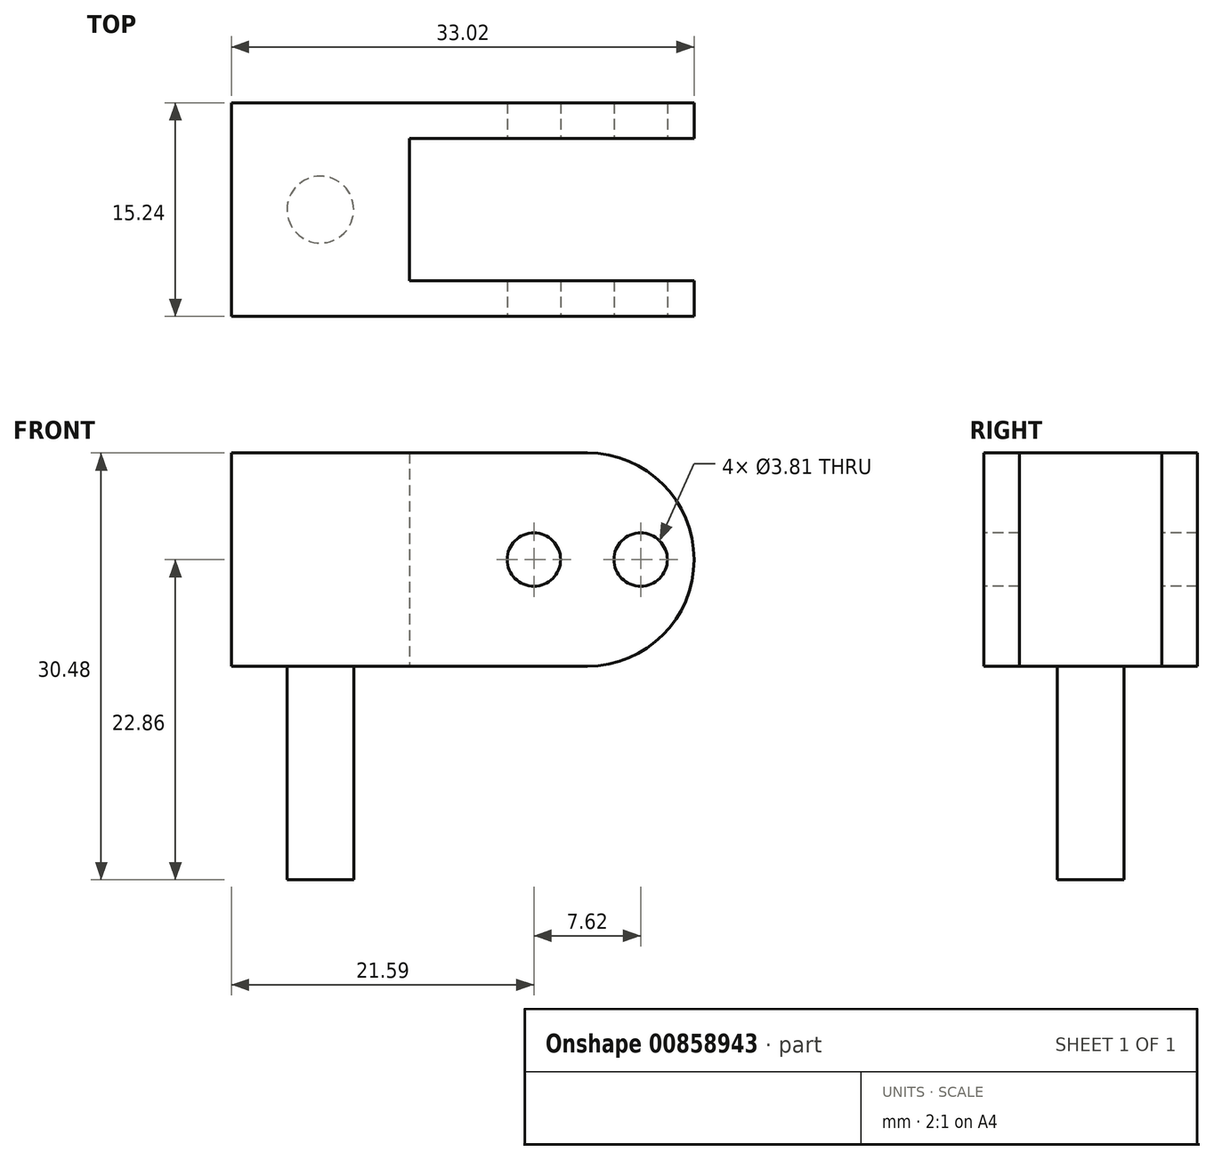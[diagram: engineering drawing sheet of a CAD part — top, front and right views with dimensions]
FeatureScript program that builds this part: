
annotation { "Feature Type Name" : "Feature", "Feature Type Description" : "" }
export const myFeature = defineFeature(function(context is Context, id is Id, definition is map)
    precondition{}
    {
        {
            var Q0;
            Q0=qCreatedBy(makeId("Top.planeOp"),FACE);
            var sketch = newSketch(context, id + "F0", { "sketchPlane" : qUnion([Q0])});
            skLineSegment(sketch, "E0.bottom", {"start": v(6.35, 7.62) * mm, "end": v(-6.35, 7.62) * mm});
            skLineSegment(sketch, "E0.top", {"start": v(6.35, -7.62) * mm, "end": v(-6.35, -7.62) * mm});
            skLineSegment(sketch, "E0.left", {"start": v(6.35, 7.62) * mm, "end": v(6.35, -7.62) * mm});
            skLineSegment(sketch, "E0.right", {"start": v(-6.35, 7.62) * mm, "end": v(-6.35, -7.62) * mm});
            skPoint(sketch, "E0.middle", {"position": v(0, 0) * mm});
            skSolve(sketch);
        }
        {
            var Q0;
            Q0=qSketchRegion(id+"F0",true);
            extrude(context, id + "F1", {"entities" : qUnion([Q0]), "depth" : 15.24 * mm, "offsetDistance" : 25.4 * mm});
        }
        {
            var Q0;
            Q0=makeQuery(id+"F1.opExtrude","CAP_FACE",FACE,{"disambiguationData":[OSD([sQuery(id+"F0.wireOp",EDGE,"E0.bottom"),sQuery(id+"F0.wireOp",EDGE,"E0.top"),sQuery(id+"F0.wireOp",EDGE,"E0.left"),sQuery(id+"F0.wireOp",EDGE,"E0.right")])],"isStart":true});
            var sketch = newSketch(context, id + "F2", { "sketchPlane" : qUnion([Q0])});
            skCircle(sketch, "E1", {"center": v(0, 0) * mm, "radius": 2.38 * mm});
            skSolve(sketch);
        }
        {
            var Q0;
            Q0=qSketchRegion(id+"F2",true);
            extrude(context, id + "F3", {"entities" : qUnion([Q0]), "operationType" : NewBodyOperationType.ADD, "depth" : 15.24 * mm, "offsetDistance" : 25.4 * mm});
        }
        {
            var Q0;
            Q0=makeQuery(id+"F1.opExtrude","SWEPT_FACE",FACE,{"disambiguationData":[OSD([sQuery(id+"F0.wireOp",EDGE,"E0.top")])]});
            var sketch = newSketch(context, id + "F4", { "sketchPlane" : qUnion([Q0])});
            skLineSegment(sketch, "E2.bottom", {"start": v(6.35, 15.24) * mm, "end": v(19.05, 15.24) * mm});
            skLineSegment(sketch, "E2.top", {"start": v(6.35, 0) * mm, "end": v(19.05, 0) * mm});
            skLineSegment(sketch, "E2.left", {"start": v(6.35, 15.24) * mm, "end": v(6.35, 0) * mm});
            skLineSegment(sketch, "E2.right", {"start": v(19.05, 15.24) * mm, "end": v(19.05, 0) * mm});
            skArc(sketch, "E3", {"start": v(19.05, 0) * mm, "mid": v(26.67, 7.62) * mm, "end": v(19.05, 15.24) * mm});
            skSolve(sketch);
        }
        {
            var Q0;
            Q0=makeQuery(id+"F4.imprint","IMPRINT",FACE,{"disambiguationData":[TD([[makeQuery(id+"F4.imprint","IMPRINT",EDGE,{"derivedFrom":sQuery(id+"F4.wireOp",EDGE,"E2.bottom")}),-1.0]])]});
            var Q1;
            Q1=makeQuery(id+"F4.imprint","IMPRINT",FACE,{"disambiguationData":[TD([[makeQuery(id+"F4.imprint","IMPRINT",EDGE,{"derivedFrom":sQuery(id+"F4.wireOp",EDGE,"E2.right")}),1.0]])]});
            extrude(context, id + "F5", {"entities" : qUnion([Q0, Q1]), "operationType" : NewBodyOperationType.ADD, "oppositeDirection" : true, "depth" : 2.54 * mm, "offsetDistance" : 25.4 * mm});
        }
        {
            var Q0;
            Q0=makeQuery(id+"F1.opExtrude","SWEPT_BODY",BODY,{"disambiguationData":[OSD([sQuery(id+"F0.wireOp",EDGE,"E0.bottom"),sQuery(id+"F0.wireOp",EDGE,"E0.top"),sQuery(id+"F0.wireOp",EDGE,"E0.left"),sQuery(id+"F0.wireOp",EDGE,"E0.right")])]});
            var Q1;
            Q1=qCreatedBy(makeId("Front.planeOp"),FACE);
            mirror(context, id + "F6", {"operationType" : NewBodyOperationType.ADD, "entities" : qUnion([Q0]), "mirrorPlane" : qUnion([Q1])});
        }
        {
            var Q0;
            Q0=makeQuery(id+"F5.boolean.opBoolean","MERGE",FACE,{"derivedFrom":[makeQuery(id+"F1.opExtrude","SWEPT_FACE",FACE,{"disambiguationData":[OSD([sQuery(id+"F0.wireOp",EDGE,"E0.top")])]}),makeQuery(id+"F5.opExtrude","CAP_FACE",FACE,{"disambiguationData":[OSD([sQuery(id+"F4.wireOp",EDGE,"E2.bottom"),sQuery(id+"F4.wireOp",EDGE,"E2.top"),sQuery(id+"F4.wireOp",EDGE,"E2.left"),sQuery(id+"F4.wireOp",EDGE,"E3")])],"isStart":true})]});
            var sketch = newSketch(context, id + "F7", { "sketchPlane" : qUnion([Q0])});
            skCircle(sketch, "E4", {"center": v(15.24, 7.62) * mm, "radius": 1.9 * mm});
            skCircle(sketch, "E5", {"center": v(22.86, 7.62) * mm, "radius": 1.9 * mm});
            skSolve(sketch);
        }
        {
            var Q0;
            Q0=qSketchRegion(id+"F7",true);
            extrude(context, id + "F8", {"entities" : qUnion([Q0]), "operationType" : NewBodyOperationType.REMOVE, "endBound" : BoundingType.THROUGH_ALL, "oppositeDirection" : true, "depth" : 25.4 * mm, "offsetDistance" : 25.4 * mm});
        }
    });
